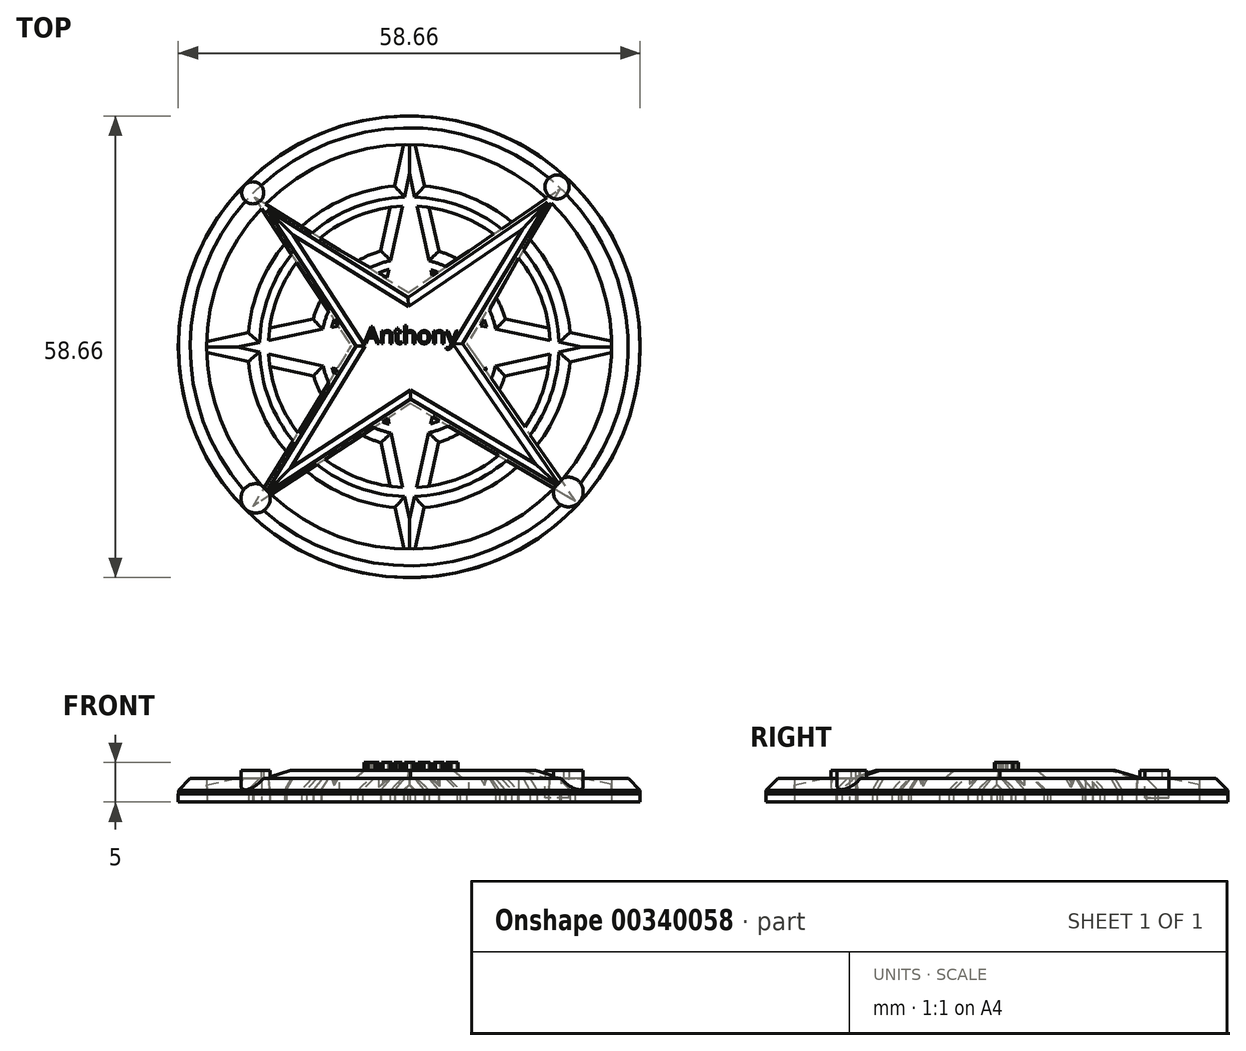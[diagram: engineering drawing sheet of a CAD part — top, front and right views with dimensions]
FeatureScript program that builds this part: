
annotation { "Feature Type Name" : "Feature", "Feature Type Description" : "" }
export const myFeature = defineFeature(function(context is Context, id is Id, definition is map)
    precondition{}
    {
        {
            var Q0;
            Q0=qCreatedBy(makeId("Top.planeOp"),FACE);
            var sketch = newSketch(context, id + "F0", { "sketchPlane" : qUnion([Q0])});
            skCircle(sketch, "E0", {"center": v(0, 0) * mm, "radius": 20.51 * mm});
            skCircle(sketch, "E1", {"center": v(0, 0) * mm, "radius": 17.88 * mm});
            skSolve(sketch);
        }
        {
            var Q0;
            Q0=makeQuery(id+"F0.imprint","IMPRINT",FACE,{"disambiguationData":[TD([[makeQuery(id+"F0.imprint","IMPRINT",EDGE,{"derivedFrom":sQuery(id+"F0.wireOp",EDGE,"E0")}),1.0]])]});
            extrude(context, id + "F1", {"entities" : qUnion([Q0]), "depth" : 3 * mm});
        }
        {
            var Q0;
            Q0=qCreatedBy(makeId("Top.planeOp"),FACE);
            var sketch = newSketch(context, id + "F2", { "sketchPlane" : qUnion([Q0])});
            skCircle(sketch, "E2", {"center": v(0, 0) * mm, "radius": 25.71 * mm});
            skCircle(sketch, "E3", {"center": v(0, 0) * mm, "radius": 29.32 * mm});
            skSolve(sketch);
        }
        {
            var Q0;
            Q0=makeQuery(id+"F2.imprint","IMPRINT",FACE,{"disambiguationData":[TD([[makeQuery(id+"F2.imprint","IMPRINT",EDGE,{"derivedFrom":sQuery(id+"F2.wireOp",EDGE,"E2")}),-1.0]])]});
            extrude(context, id + "F3", {"entities" : qUnion([Q0]), "depth" : 3 * mm});
        }
        {
            var Q0;
            Q0=qCreatedBy(makeId("Top.planeOp"),FACE);
            var sketch = newSketch(context, id + "F4", { "sketchPlane" : qUnion([Q0])});
            skCircle(sketch, "E4", {"center": v(0, 0) * mm, "radius": 12.7 * mm});
            skCircle(sketch, "E5", {"center": v(0, 0) * mm, "radius": 10.16 * mm});
            skSolve(sketch);
        }
        {
            var Q0;
            Q0=makeQuery(id+"F4.imprint","IMPRINT",FACE,{"disambiguationData":[TD([[makeQuery(id+"F4.imprint","IMPRINT",EDGE,{"derivedFrom":sQuery(id+"F4.wireOp",EDGE,"E4")}),1.0]])]});
            extrude(context, id + "F5", {"entities" : qUnion([Q0]), "depth" : 3 * mm});
        }
        {
            var Q0;
            Q0=qCreatedBy(makeId("Top.planeOp"),FACE);
            var sketch = newSketch(context, id + "F6", { "sketchPlane" : qUnion([Q0])});
            skCircle(sketch, "E6", {"center": v(0, 0) * mm, "radius": 6.3 * mm});
            skSolve(sketch);
        }
        {
            var Q0;
            Q0=makeQuery(id+"F6.imprint","IMPRINT",FACE,{"disambiguationData":[TD([[makeQuery(id+"F6.imprint","IMPRINT",EDGE,{"derivedFrom":sQuery(id+"F6.wireOp",EDGE,"E6")}),1.0]])]});
            extrude(context, id + "F7", {"entities" : qUnion([Q0]), "depth" : 3 * mm});
        }
        {
            var Q0;
            Q0=qCreatedBy(makeId("Top.planeOp"),FACE);
            var sketch = newSketch(context, id + "F8", { "sketchPlane" : qUnion([Q0])});
            skLineSegment(sketch, "E7", {"start": v(-6.22, 0) * mm, "end": v(0, -28.89) * mm});
            skLineSegment(sketch, "E8", {"start": v(0, -28.89) * mm, "end": v(6.46, 0) * mm});
            skLineSegment(sketch, "E9", {"start": v(6.46, 0) * mm, "end": v(0, 29.1) * mm});
            skLineSegment(sketch, "E10", {"start": v(0, 29.1) * mm, "end": v(-6.22, 0) * mm});
            skLineSegment(sketch, "E11", {"start": v(0, 6.06) * mm, "end": v(29.15, 0) * mm});
            skLineSegment(sketch, "E12", {"start": v(29.15, 0) * mm, "end": v(0, -6.37) * mm});
            skLineSegment(sketch, "E13", {"start": v(0, -6.37) * mm, "end": v(-29, 0) * mm});
            skLineSegment(sketch, "E14", {"start": v(-29, 0) * mm, "end": v(0, 6.06) * mm});
            skSolve(sketch);
        }
        {
            var Q0;
            Q0 = qSketchRegion(id + "F8", true);
            extrude(context, id + "F9", {"entities" : qUnion([Q0]), "depth" : 3 * mm});
        }
        {
            var Q0;
            Q0=makeQuery(id+"F7.opExtrude","CAP_FACE",FACE,{"disambiguationData":[OSD([sQuery(id+"F6.wireOp",EDGE,"E6")])],"isStart":false});
            var sketch = newSketch(context, id + "F10", { "sketchPlane" : qUnion([Q0])});
            skLineSegment(sketch, "E15", {"start": v(4.45, -4.46) * mm, "end": v(-19.86, -20.26) * mm});
            skLineSegment(sketch, "E16", {"start": v(-19.86, -20.26) * mm, "end": v(-5.37, 3.3) * mm});
            skLineSegment(sketch, "E17", {"start": v(-5.37, 3.3) * mm, "end": v(19.17, 20.09) * mm});
            skLineSegment(sketch, "E18", {"start": v(19.17, 20.09) * mm, "end": v(4.45, -4.46) * mm});
            skLineSegment(sketch, "E19", {"start": v(-4.35, -4.56) * mm, "end": v(21.15, -19.6) * mm});
            skLineSegment(sketch, "E20", {"start": v(21.15, -19.6) * mm, "end": v(5.2, 3.58) * mm});
            skLineSegment(sketch, "E21", {"start": v(5.2, 3.58) * mm, "end": v(-19.7, 19.02) * mm});
            skLineSegment(sketch, "E22", {"start": v(-19.7, 19.02) * mm, "end": v(-4.35, -4.56) * mm});
            skSolve(sketch);
        }
        {
            var Q0;
            Q0 = qSketchRegion(id + "F10", true);
            extrude(context, id + "F11", {"entities" : qUnion([Q0]), "depth" : 1 * mm});
        }
        {
            var Q0;
            Q0=makeQuery(id+"F3.opExtrude","CAP_FACE",FACE,{"disambiguationData":[OSD([sQuery(id+"F2.wireOp",EDGE,"E2"),sQuery(id+"F2.wireOp",EDGE,"E3")])],"isStart":false});
            var sketch = newSketch(context, id + "F12", { "sketchPlane" : qUnion([Q0])});
            skCircle(sketch, "E23", {"center": v(-19.88, 19.56) * mm, "radius": 1.4 * mm});
            skCircle(sketch, "E24", {"center": v(-19.51, -19.25) * mm, "radius": 1.86 * mm});
            skCircle(sketch, "E25", {"center": v(20.2, -18.45) * mm, "radius": 1.9 * mm});
            skCircle(sketch, "E26", {"center": v(1.12, 27.96) * mm, "radius": 1.34 * mm});
            skCircle(sketch, "E27", {"center": v(18.77, 20.31) * mm, "radius": 1.53 * mm});
            skSolve(sketch);
        }
        {
            var Q0;
            {var subQ0=sQuery(id+"F12.wireOp",EDGE,"E24");var subQ1=makeQuery(id+"F3.opExtrude","CAP_EDGE",EDGE,{"disambiguationData":[OSD([sQuery(id+"F2.wireOp",EDGE,"E2")])],"isStart":false});var subQ2=makeQuery(id+"F12.imprint","INTERSECT",VERTEX,{"disambiguationData":[OD(0.0)],"derivedFrom":[subQ1,subQ0]});Q0=makeQuery(id+"F12.imprint","IMPRINT",FACE,{"disambiguationData":[TD([[makeQuery(id+"F12.imprint","IMPRINT",EDGE,{"disambiguationData":[TD([[subQ2,-1.0]])],"derivedFrom":subQ0}),1.0]])]});}
            var Q1;
            {var subQ0=sQuery(id+"F12.wireOp",EDGE,"E25");var subQ1=makeQuery(id+"F3.opExtrude","CAP_EDGE",EDGE,{"disambiguationData":[OSD([sQuery(id+"F2.wireOp",EDGE,"E2")])],"isStart":false});var subQ2=makeQuery(id+"F12.imprint","INTERSECT",VERTEX,{"disambiguationData":[OD(0.0)],"derivedFrom":[subQ1,subQ0]});Q1=makeQuery(id+"F12.imprint","IMPRINT",FACE,{"disambiguationData":[TD([[makeQuery(id+"F12.imprint","IMPRINT",EDGE,{"disambiguationData":[TD([[subQ2,-1.0]])],"derivedFrom":subQ0}),1.0]])]});}
            var Q2;
            Q2=makeQuery(id+"F12.imprint","IMPRINT",FACE,{"disambiguationData":[TD([[makeQuery(id+"F12.imprint","IMPRINT",EDGE,{"derivedFrom":sQuery(id+"F12.wireOp",EDGE,"E27")}),1.0]])]});
            var Q3;
            Q3=makeQuery(id+"F12.imprint","IMPRINT",FACE,{"disambiguationData":[TD([[makeQuery(id+"F12.imprint","IMPRINT",EDGE,{"derivedFrom":sQuery(id+"F12.wireOp",EDGE,"E23")}),1.0]])]});
            extrude(context, id + "F13", {"entities" : qUnion([Q0, Q1, Q2, Q3]), "depth" : 1 * mm});
        }
        {
            var Q0;
            Q0=makeQuery(id+"F11.opExtrude","CAP_FACE",FACE,{"disambiguationData":[OSD([sQuery(id+"F10.wireOp",EDGE,"E15"),sQuery(id+"F10.wireOp",EDGE,"E16"),sQuery(id+"F10.wireOp",EDGE,"E17"),sQuery(id+"F10.wireOp",EDGE,"E18"),sQuery(id+"F10.wireOp",EDGE,"E19"),sQuery(id+"F10.wireOp",EDGE,"E20"),sQuery(id+"F10.wireOp",EDGE,"E21"),sQuery(id+"F10.wireOp",EDGE,"E22")])],"isStart":false});
            var sketch = newSketch(context, id + "F14", { "sketchPlane" : qUnion([Q0])});
            skText(sketch, "E28", { "text": "Anthony ", "fontName": "OpenSans-Regular.ttf"});
            const initialGuessF14  = {"E28": [-0.00572, 0.0004, 1, 0, 0.00218]};
            skSetInitialGuess(sketch, initialGuessF14);
            skSolve(sketch);
        }
        {
            var Q0;
            Q0 = qSketchRegion(id + "F14", true);
            extrude(context, id + "F15", {"entities" : qUnion([Q0]), "operationType" : NewBodyOperationType.ADD, "depth" : 1 * mm});
        }
        {
            var Q0;
            Q0=makeQuery(id+"F11.opExtrude","CAP_FACE",FACE,{"disambiguationData":[OSD([sQuery(id+"F10.wireOp",EDGE,"E15"),sQuery(id+"F10.wireOp",EDGE,"E16"),sQuery(id+"F10.wireOp",EDGE,"E17"),sQuery(id+"F10.wireOp",EDGE,"E18"),sQuery(id+"F10.wireOp",EDGE,"E19"),sQuery(id+"F10.wireOp",EDGE,"E20"),sQuery(id+"F10.wireOp",EDGE,"E21"),sQuery(id+"F10.wireOp",EDGE,"E22")])],"isStart":true});
            extrude(context, id + "F16", {"entities" : qUnion([Q0]), "depth" : 3 * mm});
        }
        {
            var Q0;
            Q0=qCreatedBy(makeId("Top.planeOp"),FACE);
            var sketch = newSketch(context, id + "F17", { "sketchPlane" : qUnion([Q0])});
            skCircle(sketch, "E29", {"center": v(0, 0) * mm, "radius": 29.33 * mm});
            skSolve(sketch);
        }
        {
            var Q0;
            Q0=makeQuery(id+"F17.imprint","IMPRINT",FACE,{"disambiguationData":[TD([[makeQuery(id+"F17.imprint","IMPRINT",EDGE,{"derivedFrom":sQuery(id+"F17.wireOp",EDGE,"E29")}),1.0]])]});
            extrude(context, id + "F18", {"entities" : qUnion([Q0]), "depth" : 1 * mm});
        }
        {
            var Q0;
            Q0=makeQuery(id+"F13.opExtrude","CAP_FACE",FACE,{"disambiguationData":[OSD([sQuery(id+"F2.wireOp",EDGE,"E2"),sQuery(id+"F12.wireOp",EDGE,"E24")])],"isStart":true});
            extrude(context, id + "F19", {"entities" : qUnion([Q0]), "depth" : 2.3 * mm});
        }
        {
            var Q0;
            Q0=makeQuery(id+"F13.opExtrude","CAP_FACE",FACE,{"disambiguationData":[OSD([sQuery(id+"F2.wireOp",EDGE,"E2"),sQuery(id+"F12.wireOp",EDGE,"E25")])],"isStart":true});
            extrude(context, id + "F20", {"entities" : qUnion([Q0]), "depth" : 2.06 * mm});
        }
        {
            var Q0;
            Q0=makeQuery(id+"F13.opExtrude","CAP_FACE",FACE,{"disambiguationData":[OSD([sQuery(id+"F12.wireOp",EDGE,"E27")])],"isStart":true});
            extrude(context, id + "F21", {"entities" : qUnion([Q0]), "depth" : 2.5 * mm});
        }
        {
            var Q0;
            Q0=makeQuery(id+"F11.opExtrude","CAP_EDGE",EDGE,{"disambiguationData":[OSD([sQuery(id+"F10.wireOp",EDGE,"E16")])],"isStart":false});
            var Q1;
            Q1=makeQuery(id+"F11.opExtrude","CAP_EDGE",EDGE,{"disambiguationData":[OSD([sQuery(id+"F10.wireOp",EDGE,"E21")])],"isStart":false});
            var Q2;
            Q2=makeQuery(id+"F11.opExtrude","CAP_EDGE",EDGE,{"disambiguationData":[OSD([sQuery(id+"F10.wireOp",EDGE,"E22")])],"isStart":false});
            var Q3;
            Q3=makeQuery(id+"F11.opExtrude","CAP_EDGE",EDGE,{"disambiguationData":[OSD([sQuery(id+"F10.wireOp",EDGE,"E17")])],"isStart":false});
            var Q4;
            Q4=makeQuery(id+"F11.opExtrude","CAP_EDGE",EDGE,{"disambiguationData":[OSD([sQuery(id+"F10.wireOp",EDGE,"E18")])],"isStart":false});
            var Q5;
            Q5=makeQuery(id+"F11.opExtrude","CAP_EDGE",EDGE,{"disambiguationData":[OSD([sQuery(id+"F10.wireOp",EDGE,"E20")])],"isStart":false});
            var Q6;
            Q6=makeQuery(id+"F11.opExtrude","CAP_EDGE",EDGE,{"disambiguationData":[OSD([sQuery(id+"F10.wireOp",EDGE,"E19")])],"isStart":false});
            var Q7;
            Q7=makeQuery(id+"F11.opExtrude","CAP_EDGE",EDGE,{"disambiguationData":[OSD([sQuery(id+"F10.wireOp",EDGE,"E15")])],"isStart":false});
            var Q8;
            Q8=makeQuery(id+"F1.opExtrude","CAP_EDGE",EDGE,{"disambiguationData":[OSD([sQuery(id+"F0.wireOp",EDGE,"E0")])],"isStart":false});
            var Q9;
            Q9=makeQuery(id+"F9.opExtrude","CAP_EDGE",EDGE,{"disambiguationData":[OSD([sQuery(id+"F8.wireOp",EDGE,"E8")])],"isStart":false});
            var Q10;
            Q10=makeQuery(id+"F9.opExtrude","CAP_EDGE",EDGE,{"disambiguationData":[OSD([sQuery(id+"F8.wireOp",EDGE,"E7")])],"isStart":false});
            var Q11;
            Q11=makeQuery(id+"F9.opExtrude","CAP_EDGE",EDGE,{"disambiguationData":[OSD([sQuery(id+"F8.wireOp",EDGE,"E12")])],"isStart":false});
            var Q12;
            Q12=makeQuery(id+"F9.opExtrude","CAP_EDGE",EDGE,{"disambiguationData":[OSD([sQuery(id+"F8.wireOp",EDGE,"E11")])],"isStart":false});
            var Q13;
            Q13=makeQuery(id+"F9.opExtrude","CAP_EDGE",EDGE,{"disambiguationData":[OSD([sQuery(id+"F8.wireOp",EDGE,"E9")])],"isStart":false});
            var Q14;
            Q14=makeQuery(id+"F9.opExtrude","CAP_FACE",FACE,{"disambiguationData":[OSD([sQuery(id+"F8.wireOp",EDGE,"E7"),sQuery(id+"F8.wireOp",EDGE,"E8"),sQuery(id+"F8.wireOp",EDGE,"E9"),sQuery(id+"F8.wireOp",EDGE,"E10"),sQuery(id+"F8.wireOp",EDGE,"E11"),sQuery(id+"F8.wireOp",EDGE,"E12"),sQuery(id+"F8.wireOp",EDGE,"E13"),sQuery(id+"F8.wireOp",EDGE,"E14")])],"isStart":false});
            var Q15;
            Q15=makeQuery(id+"F5.opExtrude","CAP_EDGE",EDGE,{"disambiguationData":[OSD([sQuery(id+"F4.wireOp",EDGE,"E4")])],"isStart":false});
            chamfer(context, id + "F22", {"entities" : qUnion([Q0, Q1, Q2, Q3, Q4, Q5, Q6, Q7, Q8, Q9, Q10, Q11, Q12, Q13, Q14, Q15]), "width" : 1.5 * mm, "tangentPropagation" : true});
        }
        {
            var Q0;
            Q0=makeQuery(id+"F3.opExtrude","CAP_EDGE",EDGE,{"disambiguationData":[OSD([sQuery(id+"F2.wireOp",EDGE,"E3")])],"isStart":false});
            chamfer(context, id + "F23", {"entities" : qUnion([Q0]), "width" : 1.5 * mm, "tangentPropagation" : true});
        }
        {
            var Q0;
            Q0=makeQuery(id+"F16.opExtrude","CAP_FACE",FACE,{"disambiguationData":[OSD([sQuery(id+"F10.wireOp",EDGE,"E15"),sQuery(id+"F10.wireOp",EDGE,"E16"),sQuery(id+"F10.wireOp",EDGE,"E17"),sQuery(id+"F10.wireOp",EDGE,"E18"),sQuery(id+"F10.wireOp",EDGE,"E19"),sQuery(id+"F10.wireOp",EDGE,"E20"),sQuery(id+"F10.wireOp",EDGE,"E21"),sQuery(id+"F10.wireOp",EDGE,"E22")])],"isStart":true});
            var sketch = newSketch(context, id + "F24", { "sketchPlane" : qUnion([Q0])});
            skLineSegment(sketch, "E30", {"start": v(-11.5, -6.68) * mm, "end": v(-11.1, -6.99) * mm});
            skSolve(sketch);
        }
        {
            var Q0;
            Q0=makeQuery(id+"F18.opExtrude","CAP_FACE",FACE,{"disambiguationData":[OSD([sQuery(id+"F17.wireOp",EDGE,"E29")])],"isStart":false});
            var sketch = newSketch(context, id + "F25", { "sketchPlane" : qUnion([Q0])});
            skLineSegment(sketch, "E31", {"start": v(-18.6, 17.97) * mm, "end": v(-7.32, 0) * mm});
            skLineSegment(sketch, "E32", {"start": v(-7.32, 0) * mm, "end": v(-18.7, -18.86) * mm});
            skLineSegment(sketch, "E33", {"start": v(-18.7, -18.86) * mm, "end": v(0, -7.07) * mm});
            skLineSegment(sketch, "E34", {"start": v(0, -7.07) * mm, "end": v(19.76, -18.25) * mm});
            skLineSegment(sketch, "E35", {"start": v(19.76, -18.25) * mm, "end": v(7.6, 0) * mm});
            skLineSegment(sketch, "E36", {"start": v(7.6, 0) * mm, "end": v(18.44, 19.35) * mm});
            skLineSegment(sketch, "E37", {"start": v(18.44, 19.35) * mm, "end": v(0, 7.14) * mm});
            skLineSegment(sketch, "E38", {"start": v(0, 7.14) * mm, "end": v(-18.6, 17.97) * mm});
            skSolve(sketch);
        }
        {
            var Q0;
            Q0 = qSketchRegion(id + "F25", true);
            extrude(context, id + "F26", {"entities" : qUnion([Q0]), "depth" : 2 * mm});
        }
        {
            var Q0;
            {var subQ0=makeQuery(id+"F16.opExtrude","CAP_EDGE",EDGE,{"disambiguationData":[OSD([sQuery(id+"F10.wireOp",EDGE,"E15")])],"isStart":true});Q0=makeQuery(id+"F24.imprint","IMPRINT",FACE,{"disambiguationData":[TD([[makeQuery(id+"F24.imprint","IMPRINT",EDGE,{"derivedFrom":subQ0}),-1.0]])]});}
            extrude(context, id + "F27", {"entities" : qUnion([Q0]), "oppositeDirection" : true, "depth" : 2 * mm});
        }
        {
            var Q0;
            Q0=makeQuery(id+"F27.opExtrude","CAP_FACE",FACE,{"disambiguationData":[OSD([sQuery(id+"F10.wireOp",EDGE,"E15"),sQuery(id+"F10.wireOp",EDGE,"E16"),sQuery(id+"F10.wireOp",EDGE,"E17"),sQuery(id+"F10.wireOp",EDGE,"E18"),sQuery(id+"F10.wireOp",EDGE,"E19"),sQuery(id+"F10.wireOp",EDGE,"E20"),sQuery(id+"F10.wireOp",EDGE,"E21"),sQuery(id+"F10.wireOp",EDGE,"E22")])],"isStart":false});
            extrude(context, id + "F28", {"entities" : qUnion([Q0]), "depth" : 1 * mm});
        }
        {
            var Q0;
            Q0=makeQuery(id+"F27.opExtrude","CAP_FACE",FACE,{"disambiguationData":[OSD([sQuery(id+"F10.wireOp",EDGE,"E15"),sQuery(id+"F10.wireOp",EDGE,"E16"),sQuery(id+"F10.wireOp",EDGE,"E17"),sQuery(id+"F10.wireOp",EDGE,"E18"),sQuery(id+"F10.wireOp",EDGE,"E19"),sQuery(id+"F10.wireOp",EDGE,"E20"),sQuery(id+"F10.wireOp",EDGE,"E21"),sQuery(id+"F10.wireOp",EDGE,"E22")])],"isStart":false});
            extrude(context, id + "F29", {"entities" : qUnion([Q0]), "depth" : 1 * mm});
        }
        {
            var Q0;
            Q0=makeQuery(id+"F11.opExtrude","CAP_FACE",FACE,{"disambiguationData":[OSD([sQuery(id+"F10.wireOp",EDGE,"E15"),sQuery(id+"F10.wireOp",EDGE,"E16"),sQuery(id+"F10.wireOp",EDGE,"E17"),sQuery(id+"F10.wireOp",EDGE,"E18"),sQuery(id+"F10.wireOp",EDGE,"E19"),sQuery(id+"F10.wireOp",EDGE,"E20"),sQuery(id+"F10.wireOp",EDGE,"E21"),sQuery(id+"F10.wireOp",EDGE,"E22")])],"isStart":true});
            extrude(context, id + "F30", {"entities" : qUnion([Q0]), "operationType" : NewBodyOperationType.ADD, "depth" : 1 * mm});
        }
    });
